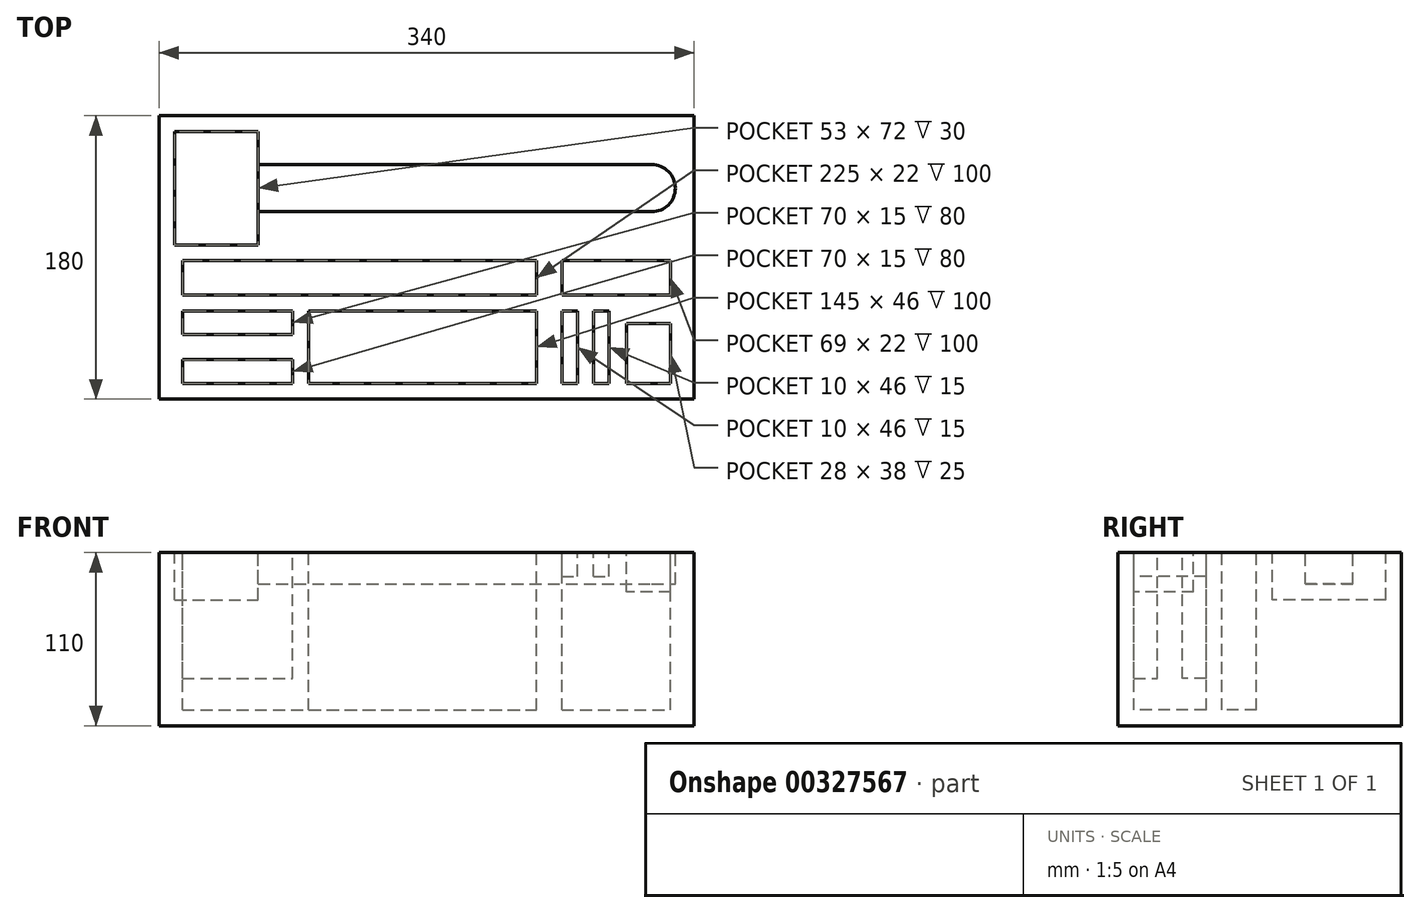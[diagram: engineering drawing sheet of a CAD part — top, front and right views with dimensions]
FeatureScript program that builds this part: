
annotation { "Feature Type Name" : "Feature", "Feature Type Description" : "" }
export const myFeature = defineFeature(function(context is Context, id is Id, definition is map)
    precondition{}
    {
        {
            var Q0;
            Q0=qCreatedBy(makeId("Top.planeOp"),FACE);
            var sketch = newSketch(context, id + "F0", { "sketchPlane" : qUnion([Q0])});
            skLineSegment(sketch, "E0.bottom", {"start": v(170, -90) * mm, "end": v(-170, -90) * mm});
            skLineSegment(sketch, "E0.top", {"start": v(170, 90) * mm, "end": v(-170, 90) * mm});
            skLineSegment(sketch, "E0.left", {"start": v(170, -90) * mm, "end": v(170, 90) * mm});
            skLineSegment(sketch, "E0.right", {"start": v(-170, -90) * mm, "end": v(-170, 90) * mm});
            skPoint(sketch, "E0.middle", {"position": v(0, 0) * mm});
            skSolve(sketch);
        }
        {
            var Q0;
            Q0 = qSketchRegion(id + "F0", true);
            extrude(context, id + "F1", {"entities" : qUnion([Q0]), "depth" : -110 * mm});
        }
        {
            var Q0;
            Q0=makeQuery(id+"F1.opExtrude","CAP_FACE",FACE,{"disambiguationData":[OSD([sQuery(id+"F0.wireOp",EDGE,"E0.bottom"),sQuery(id+"F0.wireOp",EDGE,"E0.top"),sQuery(id+"F0.wireOp",EDGE,"E0.left"),sQuery(id+"F0.wireOp",EDGE,"E0.right")])],"isStart":true});
            var sketch = newSketch(context, id + "F2", { "sketchPlane" : qUnion([Q0])});
            skLineSegment(sketch, "E1.bottom", {"start": v(-160, 80) * mm, "end": v(-107, 80) * mm});
            skLineSegment(sketch, "E1.top", {"start": v(-160, 8) * mm, "end": v(-107, 8) * mm});
            skLineSegment(sketch, "E1.left", {"start": v(-160, 80) * mm, "end": v(-160, 8) * mm});
            skLineSegment(sketch, "E1.right", {"start": v(-107, 80) * mm, "end": v(-107, 8) * mm});
            skSolve(sketch);
        }
        {
            var Q0;
            Q0=makeQuery(id+"F2.imprint","IMPRINT",FACE,{"disambiguationData":[TD([[makeQuery(id+"F2.imprint","IMPRINT",EDGE,{"derivedFrom":sQuery(id+"F2.wireOp",EDGE,"E1.bottom")}),1.0]])]});
            var sketch = newSketch(context, id + "F3", { "sketchPlane" : qUnion([Q0])});
            skLineSegment(sketch, "E2.bottom", {"start": v(-107, 59) * mm, "end": v(143, 59) * mm});
            skLineSegment(sketch, "E2.top", {"start": v(-107, 29) * mm, "end": v(143, 29) * mm});
            skLineSegment(sketch, "E2.left", {"start": v(-107, 59) * mm, "end": v(-107, 29) * mm});
            skArc(sketch, "E3", {"start": v(143, 29) * mm, "mid": v(158, 44) * mm, "end": v(143, 59) * mm});
            skLineSegment(sketch, "E4", {"start": v(143, 59) * mm, "end": v(143, 59) * mm});
            skSolve(sketch);
        }
        {
            var Q0;
            Q0=makeQuery(id+"F2.imprint","IMPRINT",FACE,{"disambiguationData":[TD([[makeQuery(id+"F2.imprint","IMPRINT",EDGE,{"derivedFrom":sQuery(id+"F2.wireOp",EDGE,"E1.bottom")}),-1.0]])]});
            extrude(context, id + "F4", {"entities" : qUnion([Q0]), "operationType" : NewBodyOperationType.REMOVE, "oppositeDirection" : true, "depth" : 30 * mm});
        }
        {
            var Q0;
            Q0=makeQuery(id+"F3.imprint","IMPRINT",FACE,{"disambiguationData":[TD([[makeQuery(id+"F3.imprint","IMPRINT",EDGE,{"derivedFrom":sQuery(id+"F3.wireOp",EDGE,"E2.bottom")}),-1.0]])]});
            extrude(context, id + "F5", {"entities" : qUnion([Q0]), "operationType" : NewBodyOperationType.REMOVE, "oppositeDirection" : true, "depth" : 20 * mm});
        }
        {
            var Q0;
            Q0=makeQuery(id+"F1.opExtrude","CAP_FACE",FACE,{"disambiguationData":[OSD([sQuery(id+"F0.wireOp",EDGE,"E0.bottom"),sQuery(id+"F0.wireOp",EDGE,"E0.top"),sQuery(id+"F0.wireOp",EDGE,"E0.left"),sQuery(id+"F0.wireOp",EDGE,"E0.right")])],"isStart":true});
            var sketch = newSketch(context, id + "F6", { "sketchPlane" : qUnion([Q0])});
            skLineSegment(sketch, "E5.bottom", {"start": v(-155, -80) * mm, "end": v(-85, -80) * mm});
            skLineSegment(sketch, "E5.top", {"start": v(-155, -65) * mm, "end": v(-85, -65) * mm});
            skLineSegment(sketch, "E5.left", {"start": v(-155, -80) * mm, "end": v(-155, -65) * mm});
            skLineSegment(sketch, "E5.right", {"start": v(-85, -80) * mm, "end": v(-85, -65) * mm});
            skLineSegment(sketch, "E6.bottom", {"start": v(-155, -34) * mm, "end": v(-85, -34) * mm});
            skLineSegment(sketch, "E6.top", {"start": v(-155, -49) * mm, "end": v(-85, -49) * mm});
            skLineSegment(sketch, "E6.left", {"start": v(-155, -34) * mm, "end": v(-155, -49) * mm});
            skLineSegment(sketch, "E6.right", {"start": v(-85, -34) * mm, "end": v(-85, -49) * mm});
            skSolve(sketch);
        }
        {
            var Q0;
            Q0=makeQuery(id+"F6.imprint","IMPRINT",FACE,{"disambiguationData":[TD([[makeQuery(id+"F6.imprint","IMPRINT",EDGE,{"derivedFrom":sQuery(id+"F6.wireOp",EDGE,"E5.bottom")}),-1.0]])]});
            var sketch = newSketch(context, id + "F7", { "sketchPlane" : qUnion([Q0])});
            skLineSegment(sketch, "E7.bottom", {"start": v(-155, -2) * mm, "end": v(70, -2) * mm});
            skLineSegment(sketch, "E7.top", {"start": v(-155, -24) * mm, "end": v(70, -24) * mm});
            skLineSegment(sketch, "E7.left", {"start": v(-155, -2) * mm, "end": v(-155, -24) * mm});
            skLineSegment(sketch, "E7.right", {"start": v(70, -2) * mm, "end": v(70, -24) * mm});
            skSolve(sketch);
        }
        {
            var Q0;
            Q0=makeQuery(id+"F6.imprint","IMPRINT",FACE,{"disambiguationData":[TD([[makeQuery(id+"F6.imprint","IMPRINT",EDGE,{"derivedFrom":sQuery(id+"F6.wireOp",EDGE,"E5.bottom")}),-1.0]])]});
            var sketch = newSketch(context, id + "F8", { "sketchPlane" : qUnion([Q0])});
            skLineSegment(sketch, "E8.bottom", {"start": v(-75, -34) * mm, "end": v(70, -34) * mm});
            skLineSegment(sketch, "E8.top", {"start": v(-75, -80) * mm, "end": v(70, -80) * mm});
            skLineSegment(sketch, "E8.left", {"start": v(-75, -34) * mm, "end": v(-75, -80) * mm});
            skLineSegment(sketch, "E8.right", {"start": v(70, -34) * mm, "end": v(70, -80) * mm});
            skSolve(sketch);
        }
        {
            var Q0;
            Q0=makeQuery(id+"F6.imprint","IMPRINT",FACE,{"disambiguationData":[TD([[makeQuery(id+"F6.imprint","IMPRINT",EDGE,{"derivedFrom":sQuery(id+"F6.wireOp",EDGE,"E5.bottom")}),-1.0]])]});
            var sketch = newSketch(context, id + "F9", { "sketchPlane" : qUnion([Q0])});
            skLineSegment(sketch, "E9.bottom", {"start": v(86, -2) * mm, "end": v(155, -2) * mm});
            skLineSegment(sketch, "E9.top", {"start": v(86, -24) * mm, "end": v(155, -24) * mm});
            skLineSegment(sketch, "E9.left", {"start": v(86, -2) * mm, "end": v(86, -24) * mm});
            skLineSegment(sketch, "E9.right", {"start": v(155, -2) * mm, "end": v(155, -24) * mm});
            skSolve(sketch);
        }
        {
            var Q0;
            Q0=makeQuery(id+"F6.imprint","IMPRINT",FACE,{"disambiguationData":[TD([[makeQuery(id+"F6.imprint","IMPRINT",EDGE,{"derivedFrom":sQuery(id+"F6.wireOp",EDGE,"E5.bottom")}),-1.0]])]});
            var sketch = newSketch(context, id + "F10", { "sketchPlane" : qUnion([Q0])});
            skLineSegment(sketch, "E10.bottom", {"start": v(86, -34) * mm, "end": v(96, -34) * mm});
            skLineSegment(sketch, "E10.top", {"start": v(86, -80) * mm, "end": v(96, -80) * mm});
            skLineSegment(sketch, "E10.left", {"start": v(86, -34) * mm, "end": v(86, -80) * mm});
            skLineSegment(sketch, "E10.right", {"start": v(96, -34) * mm, "end": v(96, -80) * mm});
            skLineSegment(sketch, "E11.bottom", {"start": v(106, -34) * mm, "end": v(116, -34) * mm});
            skLineSegment(sketch, "E11.top", {"start": v(106, -80) * mm, "end": v(116, -80) * mm});
            skLineSegment(sketch, "E11.left", {"start": v(106, -34) * mm, "end": v(106, -80) * mm});
            skLineSegment(sketch, "E11.right", {"start": v(116, -34) * mm, "end": v(116, -80) * mm});
            skSolve(sketch);
        }
        {
            var Q0;
            Q0=makeQuery(id+"F6.imprint","IMPRINT",FACE,{"disambiguationData":[TD([[makeQuery(id+"F6.imprint","IMPRINT",EDGE,{"derivedFrom":sQuery(id+"F6.wireOp",EDGE,"E5.bottom")}),-1.0]])]});
            var sketch = newSketch(context, id + "F11", { "sketchPlane" : qUnion([Q0])});
            skLineSegment(sketch, "E12.bottom", {"start": v(155, -42) * mm, "end": v(127, -42) * mm});
            skLineSegment(sketch, "E12.top", {"start": v(155, -80) * mm, "end": v(127, -80) * mm});
            skLineSegment(sketch, "E12.left", {"start": v(155, -42) * mm, "end": v(155, -80) * mm});
            skLineSegment(sketch, "E12.right", {"start": v(127, -42) * mm, "end": v(127, -80) * mm});
            skSolve(sketch);
        }
        {
            var Q0;
            Q0 = qSketchRegion(id + "F7", true);
            extrude(context, id + "F12", {"entities" : qUnion([Q0]), "operationType" : NewBodyOperationType.REMOVE, "oppositeDirection" : true, "depth" : 100 * mm});
        }
        {
            var Q0;
            Q0 = qSketchRegion(id + "F6", true);
            extrude(context, id + "F13", {"entities" : qUnion([Q0]), "operationType" : NewBodyOperationType.REMOVE, "oppositeDirection" : true, "depth" : 80 * mm});
        }
        {
            var Q0;
            Q0=makeQuery(id+"F8.imprint","IMPRINT",FACE,{"disambiguationData":[TD([[makeQuery(id+"F8.imprint","IMPRINT",EDGE,{"derivedFrom":sQuery(id+"F8.wireOp",EDGE,"E8.bottom")}),-1.0]])]});
            extrude(context, id + "F14", {"entities" : qUnion([Q0]), "operationType" : NewBodyOperationType.REMOVE, "oppositeDirection" : true, "depth" : 100 * mm});
        }
        {
            var Q0;
            Q0 = qSketchRegion(id + "F9", true);
            extrude(context, id + "F15", {"entities" : qUnion([Q0]), "operationType" : NewBodyOperationType.REMOVE, "oppositeDirection" : true, "depth" : 100 * mm});
        }
        {
            var Q0;
            Q0 = qSketchRegion(id + "F10", true);
            extrude(context, id + "F16", {"entities" : qUnion([Q0]), "operationType" : NewBodyOperationType.REMOVE, "oppositeDirection" : true, "depth" : 15 * mm});
        }
        {
            var Q0;
            Q0 = qSketchRegion(id + "F11", true);
            extrude(context, id + "F17", {"entities" : qUnion([Q0]), "operationType" : NewBodyOperationType.REMOVE, "oppositeDirection" : true, "depth" : 25 * mm});
        }
    });
